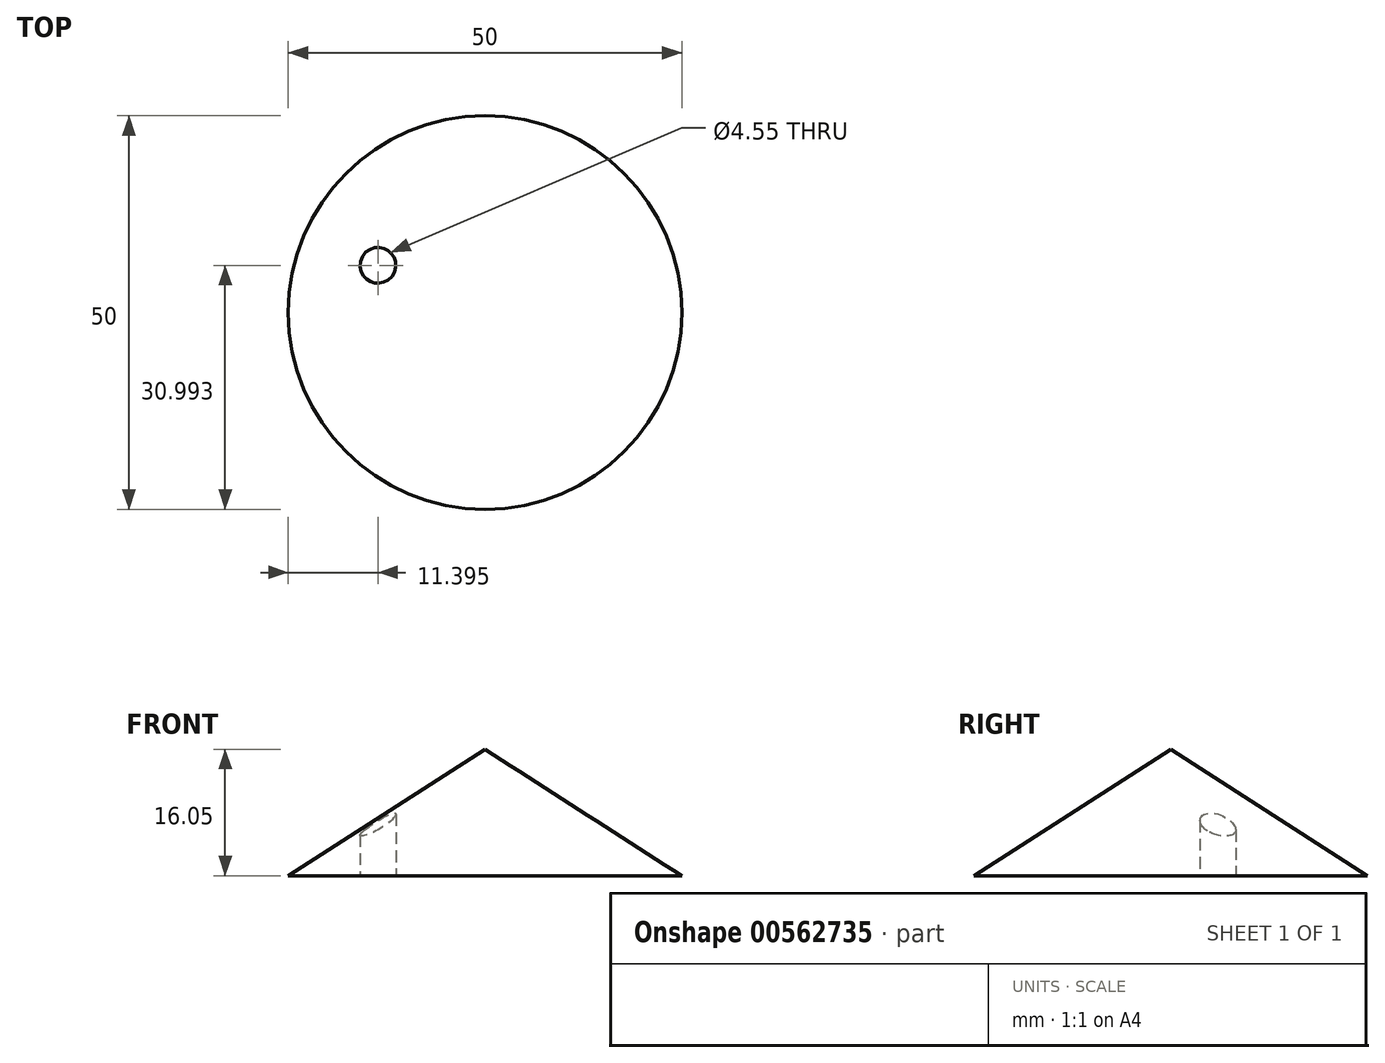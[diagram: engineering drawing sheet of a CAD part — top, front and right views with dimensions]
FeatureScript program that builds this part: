
annotation { "Feature Type Name" : "Feature", "Feature Type Description" : "" }
export const myFeature = defineFeature(function(context is Context, id is Id, definition is map)
    precondition{}
    {
        {
            var Q0;
            Q0=qCreatedBy(makeId("Top.planeOp"),FACE);
            var sketch = newSketch(context, id + "F0", { "sketchPlane" : qUnion([Q0])});
            skCircle(sketch, "E0", {"center": v(0, 0) * mm, "radius": 25 * mm});
            skSolve(sketch);
        }
        {
            var Q0;
            Q0 = qSketchRegion(id + "F0", true);
            extrude(context, id + "F1", {"entities" : qUnion([Q0]), "depth" : 30.48 * mm, "offsetDistance" : 30.48 * mm, "hasDraft" : true, "draftAngle" : 1 * radian, "draftPullDirection" : true});
        }
        {
            var Q0;
            Q0=qCreatedBy(makeId("Top.planeOp"),FACE);
            var sketch = newSketch(context, id + "F2", { "sketchPlane" : qUnion([Q0])});
            skCircle(sketch, "E1", {"center": v(-13.6, 6) * mm, "radius": 2.27 * mm});
            skSolve(sketch);
        }
        {
            var Q0;
            Q0 = qSketchRegion(id + "F2", true);
            extrude(context, id + "F3", {"entities" : qUnion([Q0]), "operationType" : NewBodyOperationType.REMOVE, "depth" : 30.48 * mm, "offsetDistance" : 30.48 * mm});
        }
    });
